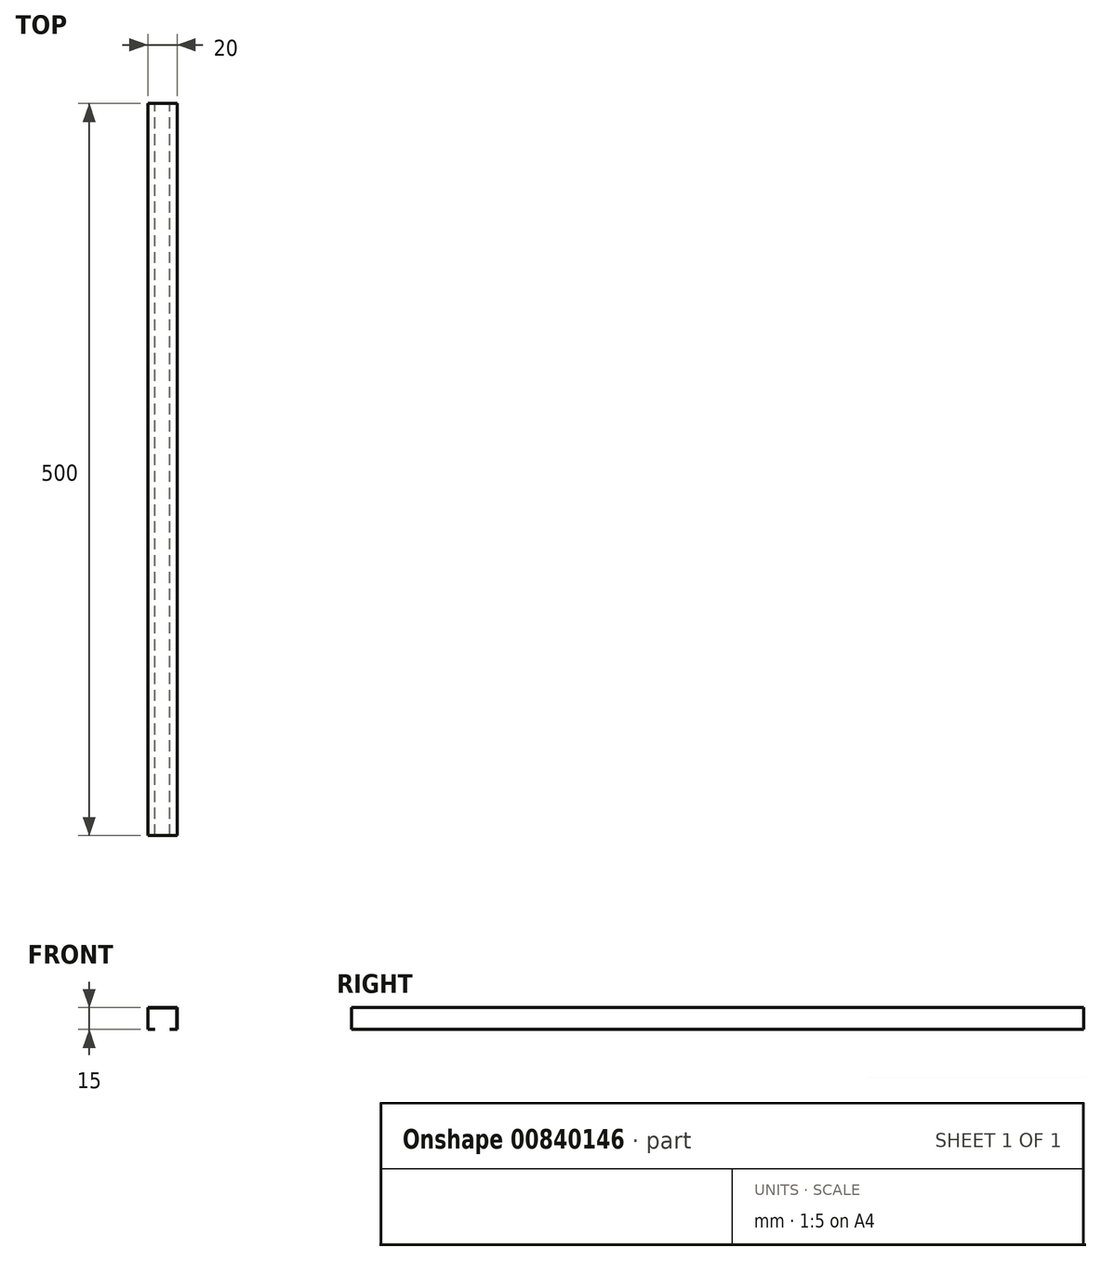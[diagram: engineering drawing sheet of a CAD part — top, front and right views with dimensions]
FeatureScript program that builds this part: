
annotation { "Feature Type Name" : "Feature", "Feature Type Description" : "" }
export const myFeature = defineFeature(function(context is Context, id is Id, definition is map)
    precondition{}
    {
        {
            var Q0;
            Q0=qCreatedBy(makeId("Front.planeOp"),FACE);
            var sketch = newSketch(context, id + "F0", { "sketchPlane" : qUnion([Q0])});
            skLineSegment(sketch, "E0.bottom", {"start": v(0, 15) * mm, "end": v(20, 15) * mm});
            skLineSegment(sketch, "E0.top", {"start": v(0, 0) * mm, "end": v(5, 0) * mm});
            skLineSegment(sketch, "E0.left", {"start": v(0, 15) * mm, "end": v(0, 0) * mm});
            skLineSegment(sketch, "E0.right", {"start": v(20, 15) * mm, "end": v(20, 0) * mm});
            skLineSegment(sketch, "E1.0", {"start": v(0.2, 14.8) * mm, "end": v(19.8, 14.8) * mm});
            skLineSegment(sketch, "E1.1", {"start": v(0.2, 14.8) * mm, "end": v(0.2, 0.2) * mm});
            skLineSegment(sketch, "E1.2", {"start": v(0.2, 0.2) * mm, "end": v(5, 0.2) * mm});
            skLineSegment(sketch, "E1.3", {"start": v(19.8, 14.8) * mm, "end": v(19.8, 0.2) * mm});
            skLineSegment(sketch, "E2", {"start": v(5, 0.2) * mm, "end": v(5, 0) * mm});
            skLineSegment(sketch, "E3", {"start": v(15, 0.2) * mm, "end": v(15, 0) * mm});
            skLineSegment(sketch, "E4.trimOffspring", {"start": v(15, 0.2) * mm, "end": v(19.8, 0.2) * mm});
            skLineSegment(sketch, "E5.trimOffspring", {"start": v(15, 0) * mm, "end": v(20, 0) * mm});
            skPoint(sketch, "E6.end.orphan", {"position": v(10, 0) * mm});
            skPoint(sketch, "E6.start.orphan", {"position": v(10, 0.2) * mm});
            skSolve(sketch);
        }
        {
            var Q0;
            Q0=makeQuery(id+"F0.imprint","IMPRINT",FACE,{"disambiguationData":[TD([[makeQuery(id+"F0.imprint","IMPRINT",EDGE,{"derivedFrom":sQuery(id+"F0.wireOp",EDGE,"E0.bottom")}),-1.0]])]});
            extrude(context, id + "F1", {"entities" : qUnion([Q0]), "depth" : 500 * mm, "offsetDistance" : 25 * mm});
        }
    });
